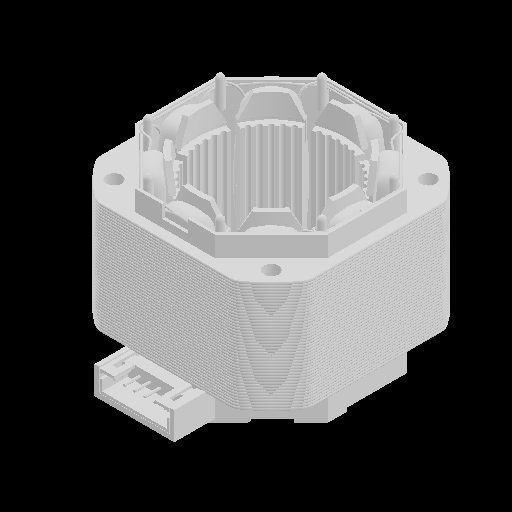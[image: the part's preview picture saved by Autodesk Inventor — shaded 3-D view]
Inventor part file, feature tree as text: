
AUTODESK INVENTOR PART (.ipt)
format: ipt  version: 2023 (Build 270158000, 158)  size: 5,531,136 bytes
history: native  units: mm
features: fillet x6, other x1
ambient origin geometry x8: Origin, YZ Plane, XZ Plane, XY Plane, X Axis, Y Axis, Z Axis, Center Point
bodies: Solid1 (feature_tree), Solid2 (feature_tree), Solid3 (feature_tree), Solid4 (feature_tree), Solid5 (feature_tree), Solid6 (feature_tree), Solid7 (feature_tree)
feature tree (7):
  fillet  "Fillet20"  [1 undecoded]
  fillet  "Fillet23"  [1 undecoded]
  other  "LPattern3"
  fillet  "Fillet9"  [1 undecoded]
  fillet  "Fillet18"  [1 undecoded]
  fillet  "Fillet29"  [1 undecoded]
  fillet  "Fillet22"  [1 undecoded]
note: 6 required parameter values undecoded (feature->parameter linkage not recoverable at this tier; creation-order binding heuristic only, values carry confidence <= 0.55)
